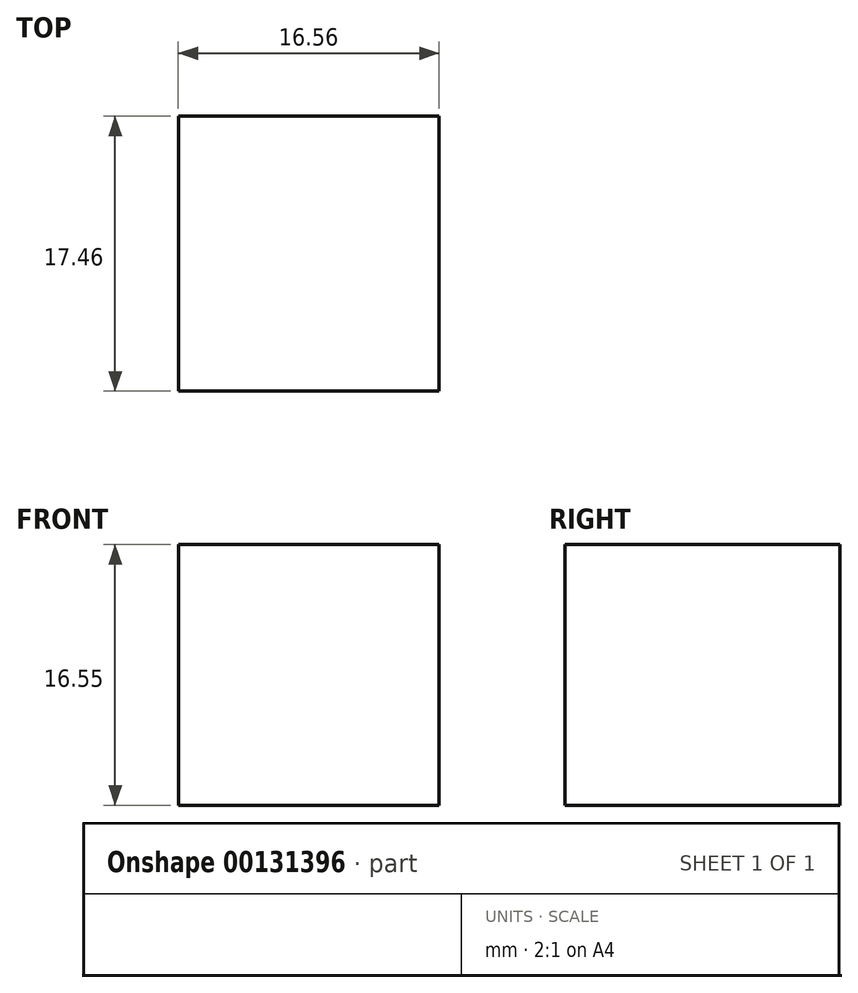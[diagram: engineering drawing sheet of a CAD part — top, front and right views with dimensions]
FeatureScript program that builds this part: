
annotation { "Feature Type Name" : "Feature", "Feature Type Description" : "" }
export const myFeature = defineFeature(function(context is Context, id is Id, definition is map)
    precondition{}
    {
        {
            var Q0;
            Q0=qCreatedBy(makeId("Front.planeOp"),FACE);
            var sketch = newSketch(context, id + "F0", { "sketchPlane" : qUnion([Q0])});
            skLineSegment(sketch, "E0.bottom", {"start": v(-38.63, 26.57) * mm, "end": v(-22.07, 26.57) * mm});
            skLineSegment(sketch, "E0.top", {"start": v(-38.63, 10.02) * mm, "end": v(-22.07, 10.02) * mm});
            skLineSegment(sketch, "E0.left", {"start": v(-38.63, 26.57) * mm, "end": v(-38.63, 10.02) * mm});
            skLineSegment(sketch, "E0.right", {"start": v(-22.07, 26.57) * mm, "end": v(-22.07, 10.02) * mm});
            skSolve(sketch);
        }
        {
            var Q0;
            Q0 = qSketchRegion(id + "F0", true);
            extrude(context, id + "F1", {"entities" : qUnion([Q0]), "endBound" : BoundingType.SYMMETRIC, "depth" : 17.46 * mm});
        }
    });
